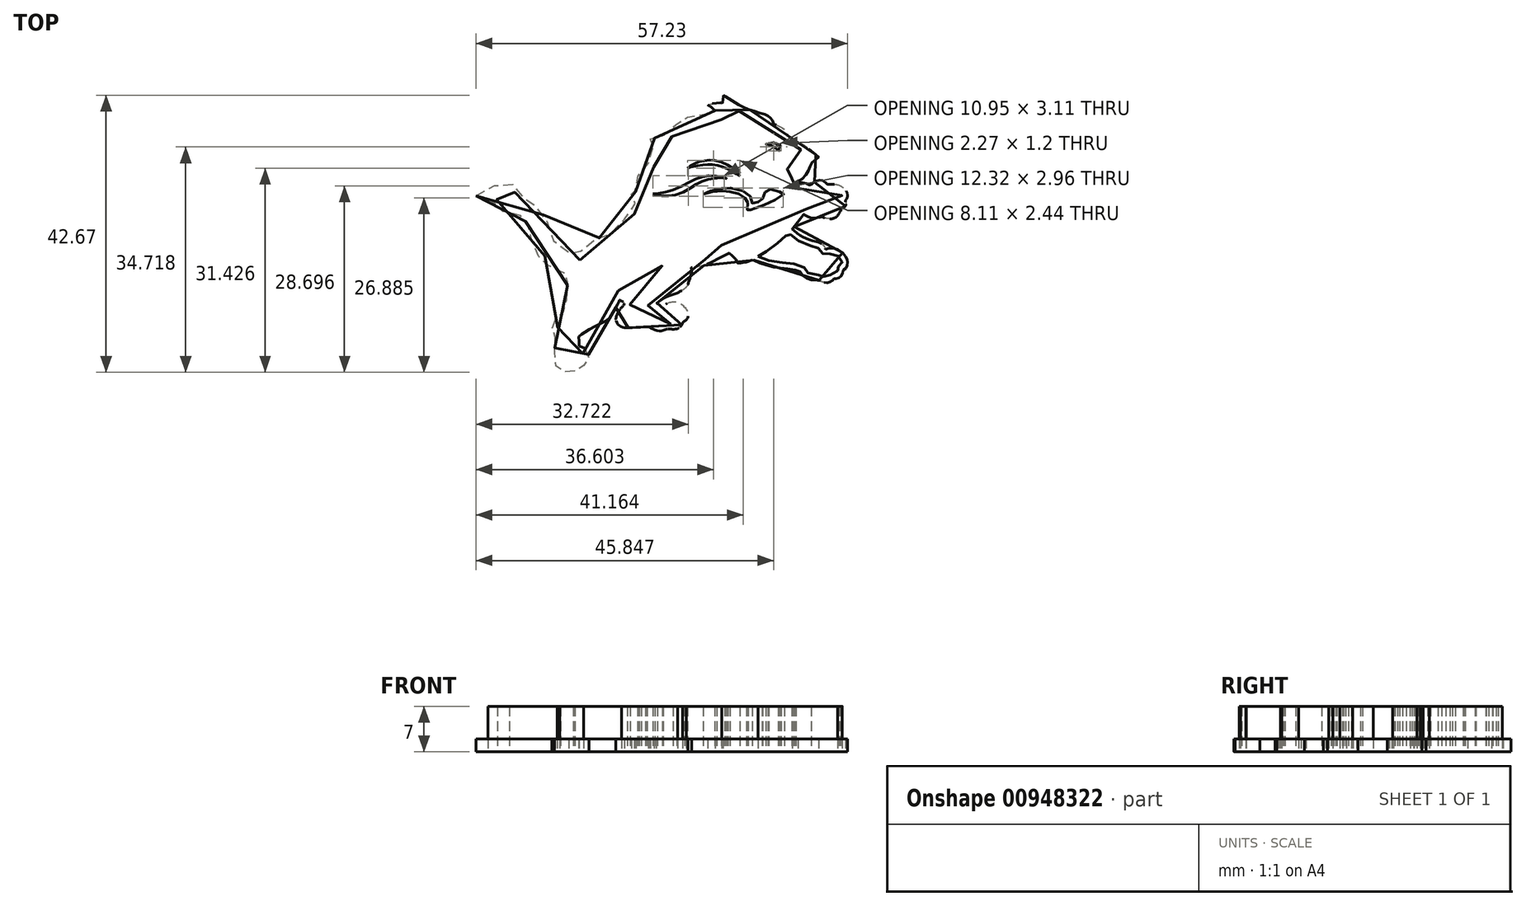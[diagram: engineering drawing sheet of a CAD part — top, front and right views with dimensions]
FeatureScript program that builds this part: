
annotation { "Feature Type Name" : "Feature", "Feature Type Description" : "" }
export const myFeature = defineFeature(function(context is Context, id is Id, definition is map)
    precondition{}
    {
        {
            var Q0;
            Q0=qCreatedBy(makeId("Top.planeOp"),FACE);
            var sketch = newSketch(context, id + "F0", { "sketchPlane" : qUnion([Q0])});
            skFitSpline(sketch, "E0", {"points": [v(-14.15, -8.38) * mm, v(-13.6, -7.75) * mm, v(-13.01, -7.16) * mm, v(-12.66, -6.84) * mm, v(-12.15, -6.4) * mm, v(-11.72, -6.07) * mm, v(-11.08, -5.82) * mm, v(-9.98, -5.48) * mm, v(-9.25, -5.2) * mm, v(-8.74, -4.8) * mm, v(-7.87, -4.1) * mm, v(-7.31, -3.62) * mm, v(-7.05, -3.39) * mm, v(-6.8, -2.92) * mm, v(-6.41, -2.37) * mm, v(-6.2, -1.96) * mm, v(-5.8, -1.31) * mm, v(-4.2, 0.7) * mm, v(-3.9, 0.92) * mm, v(-4.22, 0.92) * mm, v(-4.57, 0.98) * mm, v(-4.93, 1.13) * mm, v(-5.13, 1.24) * mm, v(-5.23, 1.36) * mm, v(-5, 1.53) * mm, v(-4.38, 1.93) * mm, v(-4.16, 2.2) * mm, v(-4.02, 2.6) * mm, v(-4.13, 2.85) * mm, v(-4.37, 2.94) * mm, v(-4.67, 2.9) * mm, v(-4.96, 2.82) * mm, v(-4.83, 3.4) * mm, v(-4.38, 4.26) * mm, v(-3.5, 5.3) * mm, v(-2.4, 6.26) * mm, v(-1.64, 6.87) * mm, v(-1.37, 7.25) * mm, v(-1.3, 7.55) * mm, v(-1.32, 7.79) * mm, v(-1.43, 7.96) * mm, v(-1.69, 8.04) * mm, v(-2.12, 7.96) * mm, v(-2.55, 7.66) * mm, v(-2.37, 8.14) * mm, v(-2.06, 8.73) * mm, v(-1.52, 9.31) * mm, v(-1.4, 9.41) * mm, v(-1.53, 9.45) * mm, v(-1.88, 9.62) * mm, v(-2.1, 9.86) * mm, v(-2.17, 9.96) * mm, v(-1.98, 9.96) * mm, v(-1.45, 10.03) * mm, v(-0.84, 10.19) * mm, v(-0.32, 10.48) * mm, v(0.73, 11.07) * mm, v(1.5, 11.44) * mm, v(1.87, 11.55) * mm, v(2.04, 11.56) * mm, v(1.86, 11.64) * mm, v(1.25, 11.66) * mm, v(0.95, 11.58) * mm, v(0.82, 11.52) * mm, v(0.97, 11.68) * mm, v(1.26, 11.97) * mm, v(1.68, 12.33) * mm, v(2.65, 12.87) * mm, v(3.44, 13.1) * mm, v(3.98, 13.2) * mm, v(5.29, 13.23) * mm, v(6.6, 13.16) * mm, v(7.07, 13.16) * mm, v(7.46, 13.2) * mm, v(7.67, 13.28) * mm, v(7.4, 13.48) * mm, v(7.05, 13.64) * mm, v(6.6, 13.65) * mm, v(6.74, 13.75) * mm, v(7.16, 14) * mm, v(8, 14.25) * mm, v(8.17, 14.22) * mm, v(7.66, 14.66) * mm, v(7.1, 14.97) * mm, v(6.93, 15.07) * mm, v(7.26, 15.06) * mm, v(7.93, 15.02) * mm, v(8.62, 14.91) * mm, v(8.98, 14.78) * mm, v(8.88, 14.96) * mm, v(8.68, 15.41) * mm, v(8.68, 15.73) * mm, v(8.84, 15.61) * mm, v(9.57, 15.1) * mm, v(10.65, 14.48) * mm, v(12.7, 13.7) * mm, v(14.05, 13.28) * mm, v(14.52, 13.04) * mm, v(14.8, 12.65) * mm, v(14.94, 12.35) * mm, v(14.9, 12.15) * mm, v(14.85, 12.08) * mm, v(14.95, 12.02) * mm, v(15.74, 11.7) * mm, v(16.5, 11.34) * mm, v(16.82, 11.15) * mm, v(17.09, 10.8) * mm, v(17.28, 10.37) * mm, v(17.45, 10.03) * mm, v(17.68, 9.73) * mm, v(18.5, 9.36) * mm, v(19.64, 8.79) * mm, v(20.58, 8.21) * mm, v(21.17, 7.77) * mm, v(21.51, 7.5) * mm, v(21.41, 7.41) * mm, v(20.98, 7.11) * mm, v(20.81, 6.94) * mm, v(20.68, 6.76) * mm, v(20.53, 6.33) * mm, v(20.36, 5.92) * mm, v(20.16, 5.48) * mm, v(19.65, 4.88) * mm, v(19.13, 4.56) * mm, v(18.95, 4.5) * mm, v(19.03, 4.66) * mm, v(19.1, 4.9) * mm, v(19.15, 5.24) * mm, v(19.13, 5.43) * mm, v(19.08, 5.65) * mm, v(19.02, 5.77) * mm, v(18.88, 5.8) * mm, v(18.5, 5.76) * mm, v(18.07, 5.74) * mm, v(17.66, 5.65) * mm, v(17.35, 5.6) * mm, v(16.63, 5.3) * mm, v(16.48, 5.22) * mm, v(16.44, 5.03) * mm, v(16.47, 4.37) * mm, v(16.7, 3.82) * mm, v(16.95, 3.6) * mm, v(17.16, 3.55) * mm, v(17.35, 3.54) * mm, v(17.62, 3.64) * mm, v(17.96, 3.87) * mm, v(18.27, 4.2) * mm, v(18.43, 4.45) * mm, v(18.5, 4.54) * mm, v(18.5, 4.38) * mm, v(18.5, 3.6) * mm, v(18.5, 3.55) * mm, v(18.59, 3.54) * mm, v(18.67, 3.55) * mm, v(18.7, 3.4) * mm, v(18.7, 2.88) * mm, v(18.67, 2.53) * mm, v(18.75, 2.55) * mm, v(18.88, 2.63) * mm, v(19.28, 2.74) * mm, v(19.66, 2.78) * mm, v(20.54, 2.62) * mm, v(21.05, 2.38) * mm, v(21.28, 2.32) * mm, v(21.5, 2.36) * mm, v(21.84, 2.54) * mm, v(22.05, 2.68) * mm, v(22.25, 2.85) * mm, v(22.5, 3.03) * mm, v(22.77, 3.1) * mm, v(23, 3.09) * mm, v(23.21, 2.95) * mm, v(23.34, 2.74) * mm, v(23.43, 2.55) * mm, v(23.52, 2.55) * mm, v(23.99, 2.53) * mm, v(24.52, 2.53) * mm, v(24.8, 2.54) * mm, v(25.13, 2.5) * mm, v(25.56, 2.32) * mm, v(25.93, 2.1) * mm, v(26.19, 1.8) * mm, v(26.26, 1.59) * mm, v(26.03, 1.28) * mm, v(25.84, 1.13) * mm, v(25.8, 1.1) * mm, v(25.83, 0.99) * mm, v(25.94, 0.73) * mm, v(25.99, 0.4) * mm, v(25.94, 0.21) * mm, v(25.76, 0.07) * mm, v(25.56, -0.03) * mm, v(25.37, -0.06) * mm, v(25.3, -0.13) * mm, v(25.23, -0.42) * mm, v(25.04, -0.77) * mm, v(24.77, -1.06) * mm, v(24.55, -1.14) * mm, v(24.27, -1.16) * mm, v(23.95, -1.09) * mm, v(23.28, -0.85) * mm, v(23.07, -0.9) * mm, v(22.53, -1.02) * mm, v(22.15, -1.06) * mm, v(21.6, -1.03) * mm, v(21.1, -0.82) * mm, v(20.81, -0.61) * mm, v(20.73, -0.49) * mm, v(20.66, -0.44) * mm, v(20.4, -0.44) * mm, v(19.98, -0.57) * mm, v(19.55, -0.92) * mm, v(18.03, -3) * mm, v(14.06, -6.46) * mm, v(12.46, -7.41) * mm, v(11.09, -7.9) * mm, v(10.8, -7.94) * mm, v(10.67, -7.98) * mm, v(10.49, -7.64) * mm, v(9.76, -6.92) * mm, v(8.87, -6.41) * mm, v(7.36, -6.03) * mm, v(5.83, -5.84) * mm, v(3.8, -5.9) * mm, v(2.39, -6.05) * mm, v(2.16, -6.09) * mm, v(2.4, -6.13) * mm, v(3.8, -6.12) * mm, v(5.74, -6.32) * mm, v(6.85, -6.6) * mm, v(7.58, -6.9) * mm, v(7.71, -6.95) * mm, v(7.52, -7.01) * mm, v(6.97, -7.36) * mm, v(5.97, -7.84) * mm, v(5.23, -8.22) * mm, v(4.39, -8.48) * mm, v(2.1, -8.74) * mm, v(2, -8.74) * mm, v(2.07, -8.97) * mm, v(2.22, -9.62) * mm, v(2.25, -10.02) * mm, v(1.95, -11.25) * mm, v(1.63, -11.93) * mm, v(1.5, -12.07) * mm, v(0.93, -12.45) * mm, v(-0.17, -12.91) * mm, v(-1.15, -13.24) * mm, v(-2.1, -13.74) * mm, v(-3.04, -14.56) * mm, v(-3.47, -15.12) * mm, v(-3.73, -15.58) * mm, v(-3.75, -15.65) * mm, v(-3.5, -15.71) * mm, v(-2.16, -15.99) * mm, v(-1.56, -16.08) * mm, v(-1.35, -16.11) * mm, v(-1.07, -16.09) * mm, v(-0.73, -15.97) * mm, v(-0.4, -15.8) * mm, v(-0.08, -15.66) * mm, v(0.28, -15.63) * mm, v(0.63, -15.66) * mm, v(1.23, -16) * mm, v(1.67, -16.68) * mm, v(1.7, -16.85) * mm, v(1.6, -17.1) * mm, v(1.23, -17.3) * mm, v(0.93, -17.37) * mm, v(0.93, -17.52) * mm, v(0.81, -18) * mm, v(0.43, -18.22) * mm, v(-0.39, -18.18) * mm, v(-0.72, -18.1) * mm, v(-0.92, -18.04) * mm, v(-0.96, -18.12) * mm, v(-1.32, -18.37) * mm, v(-1.9, -18.45) * mm, v(-2.53, -18.26) * mm, v(-2.99, -17.94) * mm, v(-3.6, -17.76) * mm, v(-5.78, -17.92) * mm, v(-7.1, -17.95) * mm, v(-7.51, -17.8) * mm, v(-7.68, -17.63) * mm, v(-7.73, -17.29) * mm, v(-7.63, -16.97) * mm, v(-7.39, -16.6) * mm, v(-6.91, -16.01) * mm, v(-6.6, -15.6) * mm, v(-6.46, -15.35) * mm, v(-6.38, -15.04) * mm, v(-6.4, -14.64) * mm, v(-6.9, -14.15) * mm, v(-7.6, -13.79) * mm, v(-7.69, -13.74) * mm, v(-7.54, -13.6) * mm, v(-7.02, -13.02) * mm, v(-6.3, -12.39) * mm, v(-5.56, -11.82) * mm, v(-2.93, -10.27) * mm, v(-1.62, -9.64) * mm, v(-0.42, -9.13) * mm, v(0.09, -8.97) * mm, v(0.25, -8.91) * mm, v(-0.08, -8.94) * mm, v(-1.37, -9.26) * mm, v(-3.33, -9.94) * mm, v(-5.48, -11.12) * mm, v(-6.46, -11.83) * mm, v(-6.72, -12.03) * mm, v(-6.8, -12.1) * mm, v(-6.77, -11.96) * mm, v(-6.52, -11.6) * mm, v(-5.73, -10.72) * mm, v(-4.78, -9.82) * mm, v(-4.69, -9.73) * mm, v(-5.08, -9.9) * mm, v(-6.46, -10.88) * mm, v(-7.18, -11.64) * mm, v(-7.92, -12.6) * mm, v(-8.28, -13.2) * mm, v(-9.06, -14.73) * mm, v(-10.04, -16.52) * mm, v(-10.3, -16.83) * mm, v(-11.13, -17.31) * mm, v(-12.22, -17.82) * mm, v(-13.35, -18.45) * mm, v(-14.73, -19.37) * mm, v(-15.03, -19.72) * mm, v(-15.12, -20.85) * mm, v(-15.02, -22.31) * mm, v(-14.9, -22.37) * mm, v(-14.53, -22.4) * mm, v(-13.97, -22.54) * mm, v(-13.7, -22.74) * mm, v(-13.57, -23.36) * mm, v(-13.66, -23.66) * mm, v(-14.11, -23.79) * mm, v(-14.23, -23.75) * mm, v(-14.25, -23.91) * mm, v(-14.34, -24.35) * mm, v(-14.66, -24.59) * mm, v(-15.19, -24.57) * mm, v(-15.45, -24.45) * mm, v(-15.54, -24.53) * mm, v(-15.97, -24.76) * mm, v(-16.43, -24.76) * mm, v(-16.83, -24.63) * mm, v(-17.16, -24.18) * mm, v(-17.2, -23.2) * mm, v(-17.09, -20) * mm, v(-17.16, -19.57) * mm, v(-17.4, -19.05) * mm, v(-17.55, -18.75) * mm, v(-17.62, -18.53) * mm, v(-17.4, -18.18) * mm, v(-16.28, -17.17) * mm, v(-15.89, -16.52) * mm, v(-15.62, -15.9) * mm, v(-15.34, -14.48) * mm, v(-15.22, -12.48) * mm, v(-15.07, -10.64) * mm, v(-14.9, -10.06) * mm, v(-14.87, -9.92) * mm, v(-15.02, -9.91) * mm, v(-16.8, -9.4) * mm, v(-18.32, -8.78) * mm, v(-19.54, -7.7) * mm, v(-20.27, -6.54) * mm, v(-20.71, -5.1) * mm, v(-20.87, -4.3) * mm, v(-21.58, -2.39) * mm, v(-22.05, -1.56) * mm, v(-22.68, -0.97) * mm, v(-23.9, -0.16) * mm, v(-23.97, -0.11) * mm, v(-24.08, -0.2) * mm, v(-24.34, -0.3) * mm, v(-24.67, -0.4) * mm, v(-24.99, -0.39) * mm, v(-25.31, -0.32) * mm, v(-26.04, 0.09) * mm, v(-26.62, 0.51) * mm, v(-26.9, 0.92) * mm, v(-27.28, 1.33) * mm, v(-27.56, 1.55) * mm, v(-28, 1.72) * mm, v(-28.26, 1.79) * mm, v(-28.03, 1.89) * mm, v(-27.53, 2.02) * mm, v(-26.65, 2.09) * mm, v(-25.82, 1.97) * mm, v(-24.96, 1.48) * mm, v(-25.02, 1.6) * mm, v(-25.13, 1.83) * mm, v(-25.51, 2.09) * mm, v(-25.82, 2.22) * mm, v(-26.31, 2.36) * mm, v(-26.8, 2.43) * mm, v(-26.73, 2.52) * mm, v(-26, 2.64) * mm, v(-25, 2.57) * mm, v(-24.23, 2.15) * mm, v(-23.73, 1.14) * mm, v(-23.62, 0.72) * mm, v(-23.18, 0.44) * mm, v(-22, -0.27) * mm, v(-20.98, -1.07) * mm, v(-20.06, -2.58) * mm, v(-19.46, -4.48) * mm, v(-18.89, -5.83) * mm, v(-17.76, -7.12) * mm, v(-16.67, -7.74) * mm, v(-15.36, -8.23) * mm, v(-14.15, -8.38) * mm]});
            skFitSpline(sketch, "E1", {"points": [v(2.42, 5.8) * mm, v(2.79, 6.1) * mm, v(3.5, 6.5) * mm, v(4.4, 6.84) * mm, v(5.46, 7) * mm, v(6.42, 7.02) * mm, v(8, 6.59) * mm, v(9.44, 5.72) * mm, v(10.26, 4.93) * mm, v(10.48, 4.65) * mm, v(10.53, 4.58) * mm, v(10.44, 4.62) * mm, v(10.26, 4.75) * mm, v(9.8, 5.07) * mm, v(8.99, 5.52) * mm, v(8.02, 5.95) * mm, v(6.87, 6.27) * mm, v(5.96, 6.38) * mm, v(5.1, 6.35) * mm, v(4.12, 6.24) * mm, v(2.66, 5.87) * mm, v(2.42, 5.8) * mm]});
            skFitSpline(sketch, "E2", {"points": [v(-2.88, 1.86) * mm, v(-2.11, 1.9) * mm, v(-1.02, 2.07) * mm, v(0.35, 2.48) * mm, v(2.34, 3.44) * mm, v(3.62, 4.11) * mm, v(4.65, 4.46) * mm, v(5.66, 4.63) * mm, v(7, 4.58) * mm, v(7.95, 4.4) * mm, v(8.44, 4.22) * mm, v(8.2, 4.28) * mm, v(7.05, 4.29) * mm, v(6.22, 4.19) * mm, v(5.29, 3.97) * mm, v(4.35, 3.6) * mm, v(3.41, 3.08) * mm, v(2.27, 2.37) * mm, v(0.64, 1.71) * mm, v(-0.55, 1.51) * mm, v(-1.53, 1.54) * mm, v(-2.4, 1.7) * mm, v(-2.72, 1.78) * mm, v(-2.88, 1.86) * mm]});
            skFitSpline(sketch, "E3", {"points": [v(4.87, 1.81) * mm, v(5.3, 2) * mm, v(5.94, 2.28) * mm, v(7.13, 2.58) * mm, v(8.3, 2.7) * mm, v(8.79, 2.74) * mm, v(10.07, 2.58) * mm, v(11.44, 2.04) * mm, v(11.92, 1.69) * mm, v(12.3, 1.1) * mm, v(12.4, 0.6) * mm, v(12.42, 0.35) * mm, v(12.56, 0.38) * mm, v(13.04, 0.48) * mm, v(13.9, 0.85) * mm, v(14, 0.9) * mm, v(13.97, 1) * mm, v(14, 1.28) * mm, v(14.1, 1.61) * mm, v(14.42, 2.15) * mm, v(14.76, 2.44) * mm, v(15.1, 2.54) * mm, v(15.64, 2.5) * mm, v(16.55, 2.2) * mm, v(17.2, 1.92) * mm, v(17.33, 1.88) * mm, v(17.3, 1.82) * mm, v(16.96, 1.56) * mm, v(15.79, 0.85) * mm, v(14.58, 0.27) * mm, v(12.52, -0.53) * mm, v(11.78, -0.76) * mm, v(11.56, -0.81) * mm, v(11.58, -0.7) * mm, v(11.74, -0.3) * mm, v(11.76, 0.3) * mm, v(11.65, 0.64) * mm, v(11.54, 0.87) * mm, v(11.38, 1.12) * mm, v(11.13, 1.39) * mm, v(10.79, 1.64) * mm, v(10.02, 1.98) * mm, v(9.2, 2.16) * mm, v(8.81, 2.23) * mm, v(8.49, 2.26) * mm, v(7.44, 2.3) * mm, v(6.51, 2.2) * mm, v(5.34, 1.96) * mm, v(4.87, 1.81) * mm]});
            skFitSpline(sketch, "E4", {"points": [v(16.85, 9.35) * mm, v(16.76, 9.36) * mm, v(16.5, 9.41) * mm, v(16.02, 9.61) * mm, v(15.8, 9.7) * mm, v(15.54, 9.7) * mm, v(14.96, 9.61) * mm, v(14.68, 9.55) * mm, v(14.54, 9.52) * mm, v(14.68, 9.48) * mm, v(15, 9.4) * mm, v(15.3, 9.32) * mm, v(15.57, 9.2) * mm, v(15.88, 8.97) * mm, v(16.44, 8.57) * mm, v(16.56, 8.48) * mm, v(16.6, 8.46) * mm, v(16.56, 8.55) * mm, v(16.5, 8.65) * mm, v(16.48, 8.77) * mm, v(16.57, 8.95) * mm, v(16.73, 9.18) * mm, v(16.85, 9.35) * mm]});
            skFitSpline(sketch, "E5", {"points": [v(13.32, -7.8) * mm, v(13.49, -7.72) * mm, v(14.14, -7.33) * mm, v(15, -6.76) * mm, v(16.18, -5.89) * mm, v(16.75, -5.39) * mm, v(17.45, -4.72) * mm, v(17.93, -4.25) * mm, v(18.02, -4.15) * mm, v(18.1, -4.25) * mm, v(18.43, -4.5) * mm, v(18.79, -4.84) * mm, v(19.43, -5.3) * mm, v(20.42, -5.79) * mm, v(21.5, -6.18) * mm, v(22.14, -6.33) * mm, v(22.42, -6.4) * mm, v(22.66, -6.57) * mm, v(22.91, -6.9) * mm, v(23.05, -7.18) * mm, v(23.3, -7.4) * mm, v(23.6, -7.5) * mm, v(24.05, -7.49) * mm, v(24.52, -7.37) * mm, v(25, -7.4) * mm, v(25.42, -7.6) * mm, v(25.82, -7.97) * mm, v(26.03, -8.24) * mm, v(26.23, -8.58) * mm, v(26.26, -8.85) * mm, v(26.2, -9.08) * mm, v(25.96, -9.24) * mm, v(25.74, -9.32) * mm, v(25.64, -9.32) * mm, v(25.59, -9.3) * mm, v(25.58, -9.39) * mm, v(25.57, -9.72) * mm, v(25.54, -10.05) * mm, v(25.45, -10.25) * mm, v(25.34, -10.37) * mm, v(25.08, -10.42) * mm, v(24.75, -10.35) * mm, v(24.6, -10.32) * mm, v(24.51, -10.26) * mm, v(24.49, -10.32) * mm, v(24.44, -10.57) * mm, v(24.23, -10.9) * mm, v(23.87, -11.01) * mm, v(23.48, -10.93) * mm, v(23.23, -10.77) * mm, v(23.08, -10.66) * mm, v(23.03, -10.6) * mm, v(22.82, -10.63) * mm, v(21.89, -10.64) * mm, v(21.24, -10.45) * mm, v(20.85, -10.19) * mm, v(20.56, -9.84) * mm, v(20.44, -9.55) * mm, v(20.4, -9.49) * mm, v(20.16, -9.4) * mm, v(19.24, -9.07) * mm, v(18.33, -8.87) * mm, v(17.4, -8.78) * mm, v(16.46, -8.67) * mm, v(14.98, -8.4) * mm, v(13.96, -8.07) * mm, v(13.32, -7.8) * mm]});
            skSolve(sketch);
        }
        {
            var Q0;
            Q0 = qSketchRegion(id + "F0", true);
            extrude(context, id + "F1", {"entities" : qUnion([Q0]), "depth" : 7 * mm, "offsetDistance" : 25 * mm});
        }
        {
            var Q0;
            Q0=qCreatedBy(makeId("Top.planeOp"),FACE);
            var sketch = newSketch(context, id + "F2", { "sketchPlane" : qUnion([Q0])});
            skFitSpline(sketch, "E6", {"points": [v(-30.13, 1.55) * mm, v(-28.62, 2.5) * mm, v(-27.05, 3.18) * mm, v(-25.72, 3.41) * mm, v(-24.37, 3.26) * mm, v(-23.44, 2.47) * mm, v(-23, 1.54) * mm, v(-22.95, 1.22) * mm, v(-22.55, 1) * mm, v(-21.17, 0.14) * mm, v(-20.07, -0.95) * mm, v(-19.24, -2.4) * mm, v(-18.74, -4.12) * mm, v(-18.12, -5.46) * mm, v(-17.24, -6.52) * mm, v(-15.29, -7.41) * mm, v(-14.63, -7.52) * mm, v(-14.53, -7.52) * mm, v(-14.22, -7.2) * mm, v(-13.2, -6.23) * mm, v(-12.3, -5.45) * mm, v(-10.97, -4.92) * mm, v(-9.79, -4.56) * mm, v(-9.62, -4.46) * mm, v(-7.75, -2.9) * mm, v(-7.66, -2.78) * mm, v(-6.47, -0.8) * mm, v(-5.9, -0.08) * mm, v(-5.54, 0.39) * mm, v(-5.49, 0.46) * mm, v(-5.6, 0.58) * mm, v(-5.94, 1.15) * mm, v(-6.18, 1.91) * mm, v(-6.14, 2.1) * mm, v(-6.05, 2.1) * mm, v(-5.56, 2.07) * mm, v(-5.5, 2.07) * mm, v(-5.59, 2.23) * mm, v(-5.74, 2.85) * mm, v(-5.63, 3.68) * mm, v(-4.83, 5.03) * mm, v(-3.6, 6.32) * mm, v(-3.55, 6.36) * mm, v(-3.59, 6.48) * mm, v(-3.53, 7.39) * mm, v(-3.1, 8.6) * mm, v(-2.79, 9.1) * mm, v(-2.67, 9.26) * mm, v(-2.7, 9.3) * mm, v(-3.08, 9.84) * mm, v(-3.24, 10.3) * mm, v(-3.22, 10.39) * mm, v(-3.06, 10.4) * mm, v(-1.64, 10.68) * mm, v(-0.54, 11.3) * mm, v(-0.1, 11.77) * mm, v(0.61, 12.5) * mm, v(1.43, 13.16) * mm, v(2.05, 13.5) * mm, v(2.73, 13.76) * mm, v(4, 14.02) * mm, v(5.17, 14.09) * mm, v(5.52, 14.05) * mm, v(5.6, 14.04) * mm, v(5.85, 14.22) * mm, v(6.7, 14.67) * mm, v(6.62, 14.73) * mm, v(6.17, 15.15) * mm, v(5.6, 15.53) * mm, v(5.55, 15.56) * mm, v(5.68, 15.59) * mm, v(6.13, 15.71) * mm, v(7.36, 15.86) * mm, v(7.78, 15.85) * mm, v(7.89, 15.85) * mm, v(7.87, 15.98) * mm, v(7.95, 16.73) * mm, v(8, 17.04) * mm, v(8.06, 17.01) * mm, v(8.4, 16.75) * mm, v(9.36, 16.16) * mm, v(10.22, 15.6) * mm, v(12.17, 14.76) * mm, v(14.37, 14.06) * mm, v(15.12, 13.61) * mm, v(15.57, 13.05) * mm, v(15.68, 12.7) * mm, v(15.7, 12.62) * mm, v(15.95, 12.52) * mm, v(17.05, 12.02) * mm, v(17.75, 11.32) * mm, v(18.1, 10.5) * mm, v(18.88, 10.1) * mm, v(20.6, 9.2) * mm, v(22.6, 7.55) * mm, v(22.63, 7.51) * mm, v(22.1, 7.1) * mm, v(21.42, 6.41) * mm, v(21.15, 5.63) * mm, v(20.64, 4.7) * mm, v(19.89, 4) * mm, v(19.55, 3.85) * mm, v(19.5, 3.84) * mm, v(19.48, 3.7) * mm, v(19.5, 3.6) * mm, v(19.63, 3.59) * mm, v(20.1, 3.56) * mm, v(20.77, 3.4) * mm, v(21.3, 3.2) * mm, v(21.35, 3.2) * mm, v(21.63, 3.4) * mm, v(21.89, 3.6) * mm, v(22.28, 3.8) * mm, v(22.73, 3.92) * mm, v(23.16, 3.92) * mm, v(23.62, 3.67) * mm, v(23.86, 3.44) * mm, v(23.94, 3.33) * mm, v(24.25, 3.34) * mm, v(24.98, 3.34) * mm, v(25.8, 3.17) * mm, v(26.48, 2.72) * mm, v(26.95, 2.16) * mm, v(27.08, 1.63) * mm, v(27, 1.17) * mm, v(26.82, 0.9) * mm, v(26.75, 0.83) * mm, v(26.76, 0.76) * mm, v(26.82, 0.22) * mm, v(26.64, -0.27) * mm, v(26, -0.74) * mm, v(25.94, -0.86) * mm, v(25.63, -1.38) * mm, v(25.12, -1.86) * mm, v(24.3, -1.99) * mm, v(23.37, -1.8) * mm, v(23.18, -1.7) * mm, v(22.92, -1.76) * mm, v(22.03, -1.88) * mm, v(21.41, -1.84) * mm, v(20.4, -1.34) * mm, v(20.35, -1.3) * mm, v(20.31, -1.33) * mm, v(19.38, -2.57) * mm, v(18.61, -3.53) * mm, v(18.59, -3.58) * mm, v(18.6, -3.62) * mm, v(19.51, -4.34) * mm, v(20.4, -4.9) * mm, v(21.44, -5.3) * mm, v(22.63, -5.6) * mm, v(23.21, -5.94) * mm, v(23.55, -6.32) * mm, v(23.7, -6.64) * mm, v(23.7, -6.69) * mm, v(23.8, -6.66) * mm, v(24.27, -6.57) * mm, v(25.02, -6.55) * mm, v(25.61, -6.76) * mm, v(26.12, -7.1) * mm, v(26.84, -7.88) * mm, v(27.08, -8.49) * mm, v(27.06, -9.13) * mm, v(26.76, -9.67) * mm, v(26.5, -9.87) * mm, v(26.4, -9.93) * mm, v(26.38, -10.1) * mm, v(26.15, -10.74) * mm, v(25.74, -11.1) * mm, v(25.27, -11.24) * mm, v(25.02, -11.24) * mm, v(24.9, -11.4) * mm, v(24.35, -11.76) * mm, v(23.82, -11.86) * mm, v(23.13, -11.7) * mm, v(22.86, -11.52) * mm, v(22.8, -11.46) * mm, v(22.64, -11.45) * mm, v(21.9, -11.44) * mm, v(21.04, -11.26) * mm, v(20.63, -11.06) * mm, v(20.15, -10.66) * mm, v(19.82, -10.16) * mm, v(19.63, -10.06) * mm, v(18.6, -9.78) * mm, v(17.14, -9.6) * mm, v(16, -9.5) * mm, v(14.68, -9.18) * mm, v(13.46, -8.76) * mm, v(12.73, -8.43) * mm, v(12.52, -8.28) * mm, v(12.42, -8.31) * mm, v(11.75, -8.58) * mm, v(10.97, -8.79) * mm, v(10.37, -8.86) * mm, v(10.22, -8.86) * mm, v(10.14, -8.69) * mm, v(9.82, -8.2) * mm, v(9.4, -7.72) * mm, v(8.99, -7.4) * mm, v(8.8, -7.27) * mm, v(8.68, -7.32) * mm, v(8, -7.7) * mm, v(6.61, -8.43) * mm, v(5.65, -8.92) * mm, v(5.1, -9.13) * mm, v(3.66, -9.43) * mm, v(3.06, -9.48) * mm, v(3.03, -9.57) * mm, v(3.06, -10.08) * mm, v(2.9, -10.83) * mm, v(2.55, -11.94) * mm, v(2.15, -12.62) * mm, v(1.4, -13.14) * mm, v(0.63, -13.5) * mm, v(-0.57, -13.9) * mm, v(-1.22, -14.22) * mm, v(-1.65, -14.5) * mm, v(-2.2, -14.9) * mm, v(-2.4, -15.07) * mm, v(-2.31, -15.12) * mm, v(-1.87, -15.21) * mm, v(-1.48, -15.28) * mm, v(-1.2, -15.26) * mm, v(-0.79, -15.08) * mm, v(-0.33, -14.89) * mm, v(0.25, -14.79) * mm, v(0.96, -14.87) * mm, v(1.53, -15.18) * mm, v(2.03, -15.68) * mm, v(2.42, -16.26) * mm, v(2.52, -16.96) * mm, v(2.25, -17.57) * mm, v(1.69, -17.98) * mm, v(1.65, -18.17) * mm, v(1.38, -18.58) * mm, v(1.01, -18.9) * mm, v(0.64, -18.98) * mm, v(0.05, -19) * mm, v(-0.69, -18.94) * mm, v(-0.85, -19.02) * mm, v(-1.38, -19.23) * mm, v(-1.76, -19.3) * mm, v(-2.18, -19.26) * mm, v(-2.76, -19.03) * mm, v(-3.32, -18.73) * mm, v(-3.51, -18.66) * mm, v(-3.69, -18.63) * mm, v(-4.16, -18.65) * mm, v(-5.7, -18.76) * mm, v(-6.64, -18.8) * mm, v(-7.21, -18.8) * mm, v(-7.5, -18.75) * mm, v(-7.81, -18.62) * mm, v(-8.06, -18.44) * mm, v(-8.28, -18.23) * mm, v(-8.5, -17.89) * mm, v(-8.59, -17.57) * mm, v(-8.53, -17.09) * mm, v(-8.4, -16.67) * mm, v(-8.1, -16.14) * mm, v(-7.67, -15.62) * mm, v(-7.33, -15.2) * mm, v(-7.3, -14.94) * mm, v(-7.6, -14.73) * mm, v(-7.96, -14.53) * mm, v(-8, -14.5) * mm, v(-8.09, -14.67) * mm, v(-8.6, -15.68) * mm, v(-9.03, -16.48) * mm, v(-9.34, -16.94) * mm, v(-9.78, -17.44) * mm, v(-10.23, -17.77) * mm, v(-12.59, -18.98) * mm, v(-14.03, -19.92) * mm, v(-14.32, -20.19) * mm, v(-14.3, -20.44) * mm, v(-14.26, -21.65) * mm, v(-14.16, -21.65) * mm, v(-13.54, -21.86) * mm, v(-13.06, -22.23) * mm, v(-12.8, -22.82) * mm, v(-12.86, -23.76) * mm, v(-13.26, -24.37) * mm, v(-13.48, -24.45) * mm, v(-13.6, -24.73) * mm, v(-14, -25.23) * mm, v(-14.64, -25.45) * mm, v(-15.22, -25.38) * mm, v(-15.91, -25.58) * mm, v(-16.76, -25.56) * mm, v(-17.4, -25.21) * mm, v(-17.8, -24.76) * mm, v(-18.03, -24.2) * mm, v(-18.04, -22.81) * mm, v(-18, -21.23) * mm, v(-17.92, -20.06) * mm, v(-18.02, -19.67) * mm, v(-18.22, -19.36) * mm, v(-18.44, -18.66) * mm, v(-18.4, -18.22) * mm, v(-18.07, -17.71) * mm, v(-17.55, -17.17) * mm, v(-17, -16.72) * mm, v(-16.6, -16.1) * mm, v(-16.32, -15.18) * mm, v(-16.15, -14.4) * mm, v(-16.09, -13.1) * mm, v(-15.9, -10.73) * mm, v(-15.87, -10.52) * mm, v(-16.1, -10.48) * mm, v(-18.2, -9.74) * mm, v(-19.4, -8.96) * mm, v(-19.84, -8.6) * mm, v(-20.63, -7.57) * mm, v(-21.29, -6.13) * mm, v(-21.66, -4.59) * mm, v(-22.03, -3.29) * mm, v(-22.48, -2.4) * mm, v(-23.03, -1.72) * mm, v(-23.88, -1.09) * mm, v(-24, -1.07) * mm, v(-24.2, -1.13) * mm, v(-24.78, -1.2) * mm, v(-25.44, -1.11) * mm, v(-25.94, -0.9) * mm, v(-26.52, -0.48) * mm, v(-27.14, 0.19) * mm, v(-27.54, 0.69) * mm, v(-27.95, 1.03) * mm, v(-28.81, 1.35) * mm, v(-29.67, 1.52) * mm, v(-29.96, 1.56) * mm, v(-30.13, 1.55) * mm]});
            skSolve(sketch);
        }
        {
            var Q0;
            Q0=makeQuery(id+"F2.imprint","IMPRINT",FACE,{"disambiguationData":[TD([[makeQuery(id+"F2.imprint","IMPRINT",EDGE,{"derivedFrom":sQuery(id+"F2.wireOp",EDGE,"E6")}),-1.0]])]});
            extrude(context, id + "F3", {"entities" : qUnion([Q0]), "depth" : 2 * mm, "offsetDistance" : 25 * mm});
        }
    });
